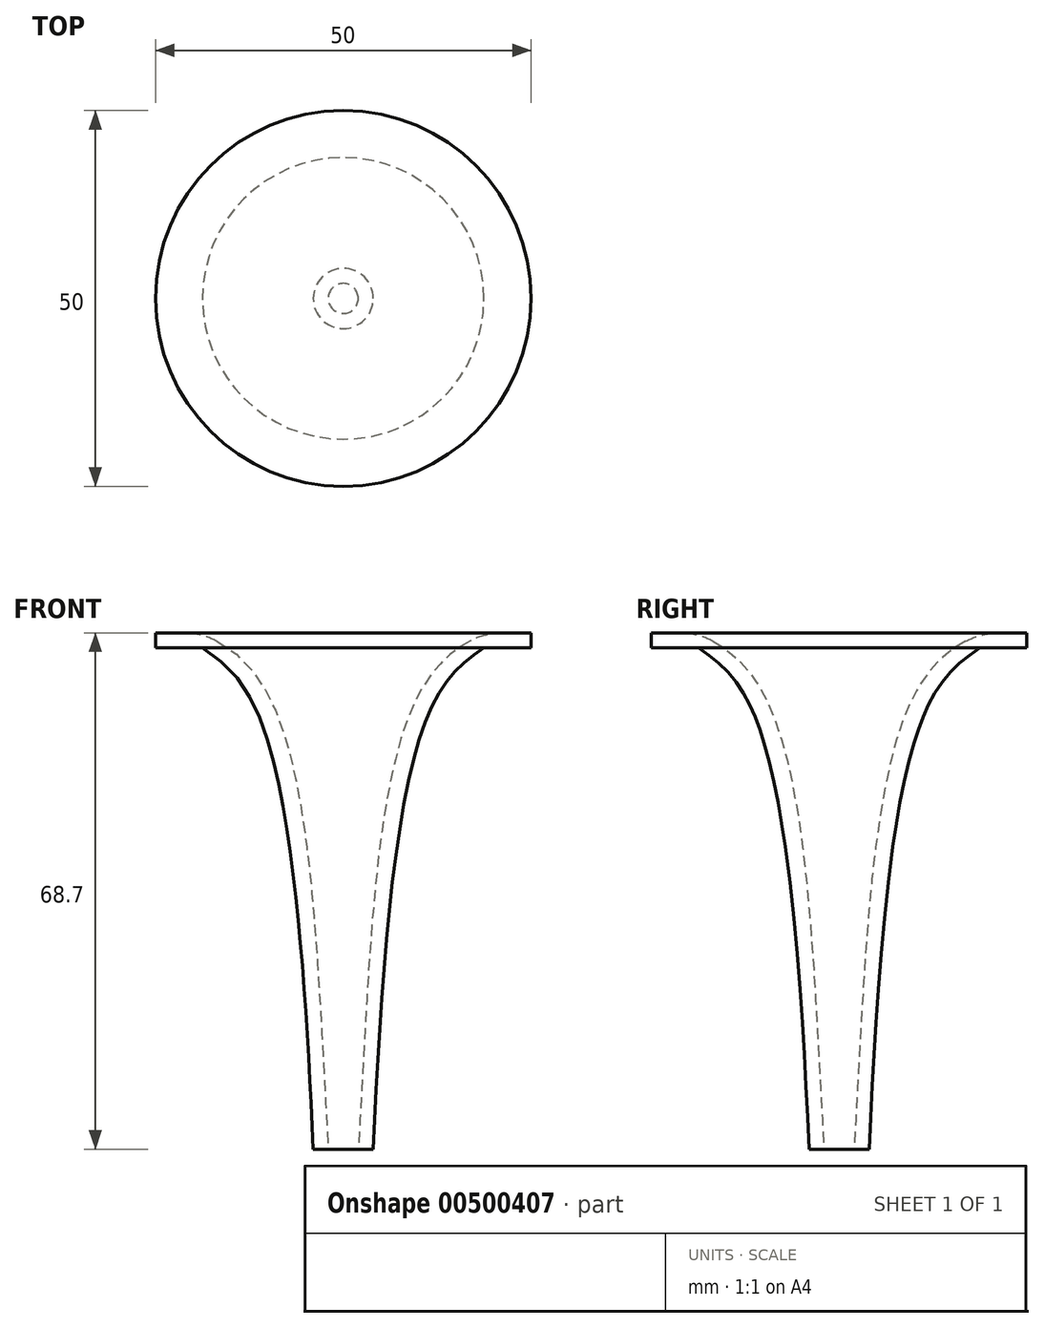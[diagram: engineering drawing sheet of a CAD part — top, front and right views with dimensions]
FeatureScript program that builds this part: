
annotation { "Feature Type Name" : "Feature", "Feature Type Description" : "" }
export const myFeature = defineFeature(function(context is Context, id is Id, definition is map)
    precondition{}
    {
        {
            var Q0;
            Q0=qCreatedBy(makeId("Front.planeOp"),FACE);
            var sketch = newSketch(context, id + "F0", { "sketchPlane" : qUnion([Q0])});
            skLineSegment(sketch, "E0", {"start": v(0, 34.35) * mm, "end": v(0, -34.35) * mm, "construction": true});
            skPoint(sketch, "E1", {"position": v(0, 0) * mm});
            skLineSegment(sketch, "E2", {"start": v(0, -34.35) * mm, "end": v(2, -34.35) * mm, "construction": true});
            skLineSegment(sketch, "E3", {"start": v(0, 34.35) * mm, "end": v(20, 34.35) * mm, "construction": true});
            skLineSegment(sketch, "E4", {"start": v(2, -34.35) * mm, "end": v(4, -34.35) * mm});
            skLineSegment(sketch, "E5", {"start": v(20, 34.35) * mm, "end": v(22, 34.35) * mm});
            skFitSpline(sketch, "E6", {"points": [v(20, 34.35) * mm, v(9.76, 25.62) * mm, v(2, -34.35) * mm], "startDerivative": vector(-32.08, -6.16) * mm, "endDerivative": vector(-6.12, -99.23) * mm});
            skFitSpline(sketch, "E7", {"points": [v(22, 34.35) * mm, v(11.57, 24.08) * mm, v(4, -34.35) * mm], "startDerivative": vector(-41.63, -24.6) * mm, "endDerivative": vector(-4.42, -97.96) * mm});
            skLineSegment(sketch, "E8.top", {"start": v(20, 34.35) * mm, "end": v(25, 34.35) * mm});
            skLineSegment(sketch, "E9.top", {"start": v(20, 32.35) * mm, "end": v(25, 32.35) * mm});
            skLineSegment(sketch, "E9.left", {"start": v(20, 34.35) * mm, "end": v(20, 32.35) * mm});
            skLineSegment(sketch, "E9.right", {"start": v(25, 34.35) * mm, "end": v(25, 32.35) * mm});
            skLineSegment(sketch, "E10", {"start": v(20, 32.35) * mm, "end": v(18.73, 32.35) * mm});
            skSolve(sketch);
        }
        {
            var Q0;
            Q0 = qSketchRegion(id + "F0", true);
            var Q1;
            Q1=sQuery(id+"F0.wireOp",EDGE,"E0");
            revolve(context, id + "F1", {"entities" : qUnion([Q0]), "axis" : qUnion([Q1]), "revolveType" : RevolveType.FULL});
        }
        {
            var Q0;
            Q0=makeQuery(id+"F1.opRevolve","SWEPT_EDGE",EDGE,{"disambiguationData":[OSD([sQuery(id+"F0.wireOp",EDGE,"E6"),sQuery(id+"F0.wireOp",EDGE,"E8.top"),sQuery(id+"F0.wireOp",EDGE,"E9.left")])]});
            fillet(context, id + "F2", {"entities" : qUnion([Q0]), "radius" : 10 * mm, "tangentPropagation" : true, "allowEdgeOverflow" : false});
        }
    });
